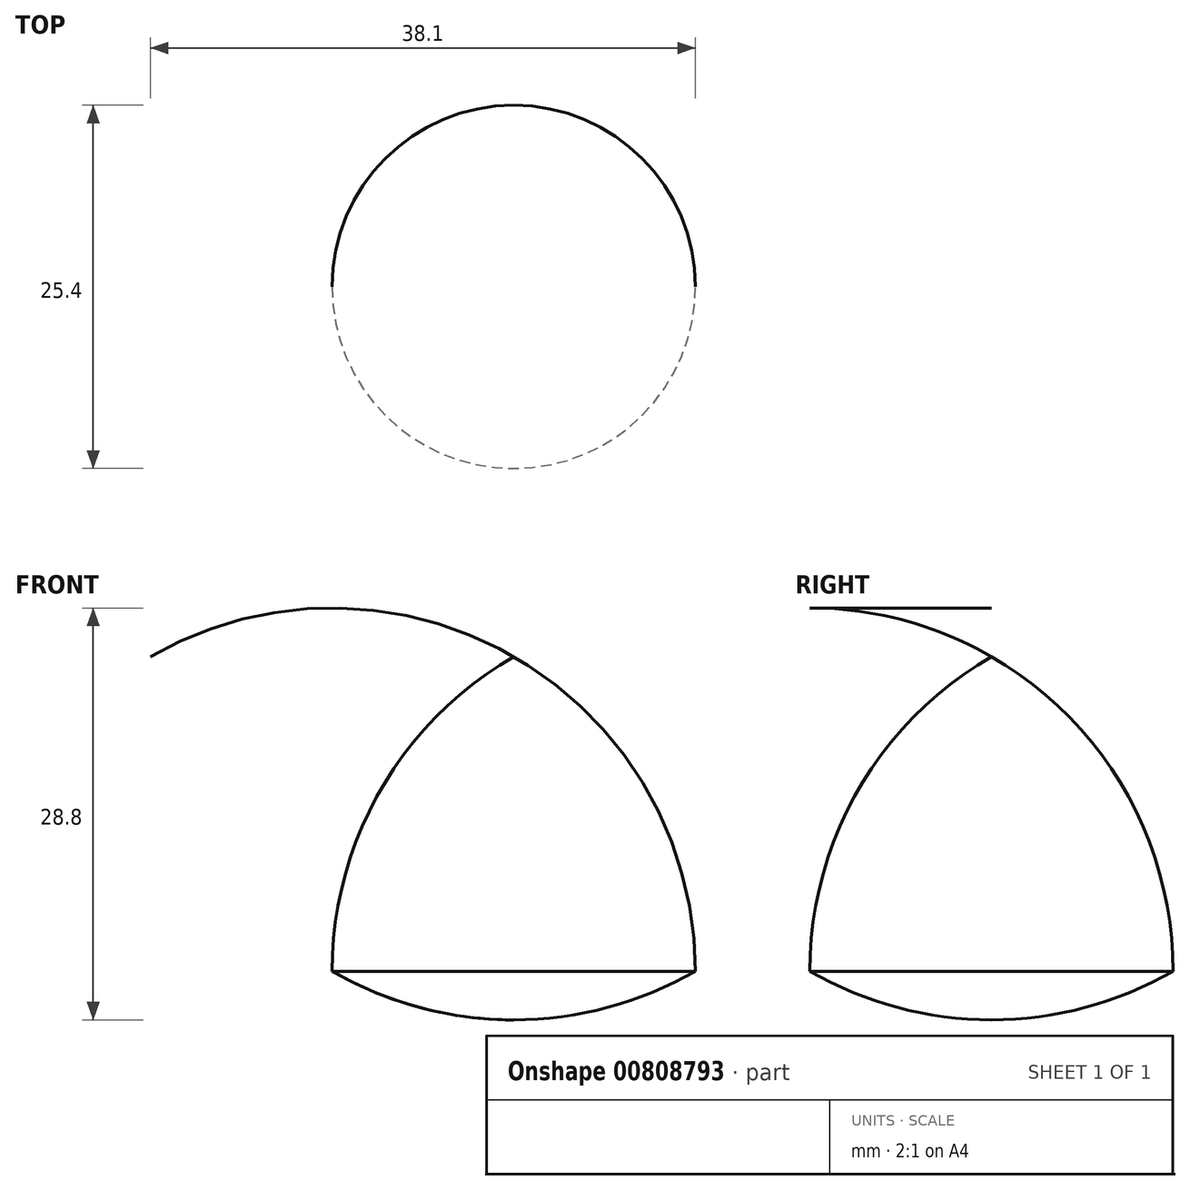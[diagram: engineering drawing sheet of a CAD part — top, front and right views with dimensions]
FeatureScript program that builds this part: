
annotation { "Feature Type Name" : "Feature", "Feature Type Description" : "" }
export const myFeature = defineFeature(function(context is Context, id is Id, definition is map)
    precondition{}
    {
        {
            var Q0;
            Q0=qCreatedBy(makeId("Front.planeOp"),FACE);
            var sketch = newSketch(context, id + "F0", { "sketchPlane" : qUnion([Q0])});
            skLineSegment(sketch, "E0", {"start": v(0, 0) * mm, "end": v(-12.7, 0) * mm});
            skLineSegment(sketch, "E1", {"start": v(-12.7, 0) * mm, "end": v(0, 22) * mm});
            skLineSegment(sketch, "E2", {"start": v(0, 22) * mm, "end": v(12.7, 0) * mm});
            skLineSegment(sketch, "E3", {"start": v(12.7, 0) * mm, "end": v(0, 0) * mm});
            skArc(sketch, "E4", {"start": v(-12.7, 0) * mm, "mid": v(0, -3.4) * mm, "end": v(12.7, 0) * mm});
            skArc(sketch, "E5", {"start": v(12.7, 0) * mm, "mid": v(9.3, 12.7) * mm, "end": v(0, 22) * mm});
            skArc(sketch, "E6", {"start": v(0, 22) * mm, "mid": v(-9.3, 12.7) * mm, "end": v(-12.7, 0) * mm});
            skLineSegment(sketch, "E7", {"start": v(0, -3.4) * mm, "end": v(0, 22) * mm});
            skSolve(sketch);
        }
        {
            var Q0;
            Q0=makeQuery(id+"F0.imprint","IMPRINT",FACE,{"disambiguationData":[TD([[makeQuery(id+"F0.imprint","IMPRINT",EDGE,{"derivedFrom":sQuery(id+"F0.wireOp",EDGE,"E2")}),1.0]])]});
            var Q1;
            {var subQ0=sQuery(id+"F0.wireOp",EDGE,"E3");Q1=makeQuery(id+"F0.imprint","IMPRINT",FACE,{"disambiguationData":[TD([[makeQuery(id+"F0.imprint","IMPRINT",EDGE,{"derivedFrom":subQ0}),1.0]])]});}
            var Q2;
            {var subQ0=sQuery(id+"F0.wireOp",EDGE,"E2");Q2=makeQuery(id+"F0.imprint","IMPRINT",FACE,{"disambiguationData":[TD([[makeQuery(id+"F0.imprint","IMPRINT",EDGE,{"derivedFrom":subQ0}),-1.0]])]});}
            var Q3;
            Q3=sQuery(id+"F0.wireOp",EDGE,"E7");
            revolve(context, id + "F1", {"surfaceOperationType" : NewSurfaceOperationType.NEW, "entities" : qUnion([Q0, Q1, Q2]), "axis" : qUnion([Q3]), "revolveType" : RevolveType.FULL});
        }
    });
